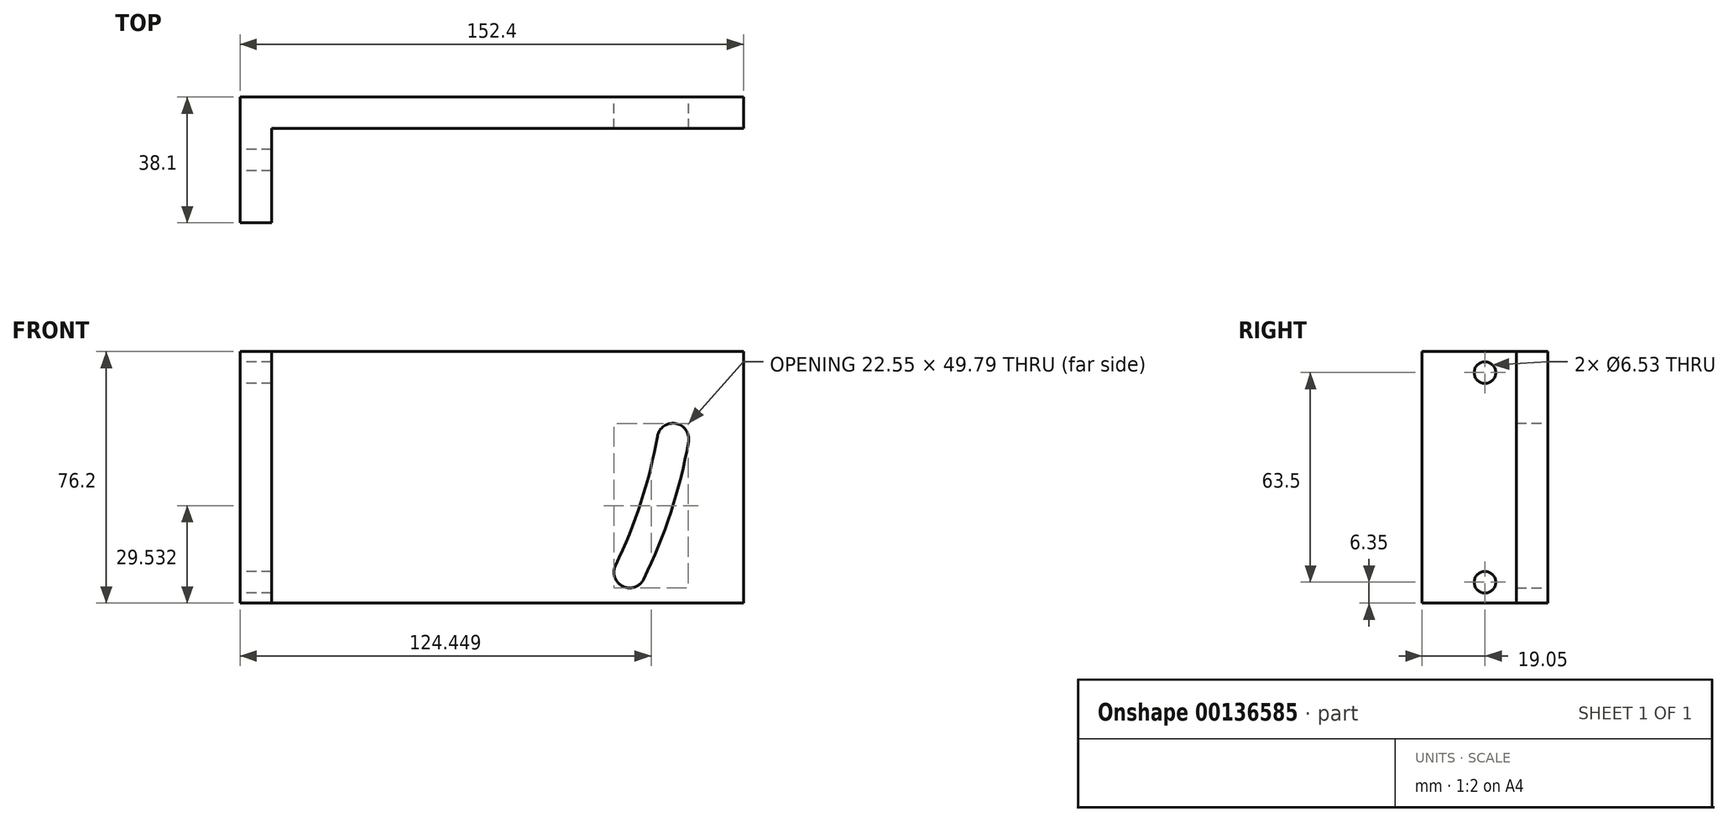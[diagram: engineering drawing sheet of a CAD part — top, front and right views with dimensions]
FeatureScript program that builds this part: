
annotation { "Feature Type Name" : "Feature", "Feature Type Description" : "" }
export const myFeature = defineFeature(function(context is Context, id is Id, definition is map)
    precondition{}
    {
        {
            var Q0;
            Q0=qCreatedBy(makeId("Front.planeOp"),FACE);
            var sketch = newSketch(context, id + "F0", { "sketchPlane" : qUnion([Q0])});
            skLineSegment(sketch, "E0.bottom", {"start": v(0, 0) * mm, "end": v(152.4, 0) * mm});
            skLineSegment(sketch, "E0.top", {"start": v(0, 76.2) * mm, "end": v(152.4, 76.2) * mm});
            skLineSegment(sketch, "E0.left", {"start": v(0, 0) * mm, "end": v(0, 76.2) * mm});
            skLineSegment(sketch, "E0.right", {"start": v(152.4, 0) * mm, "end": v(152.4, 76.2) * mm});
            skLineSegment(sketch, "E1", {"start": v(76.2, 76.2) * mm, "end": v(76.2, 0) * mm, "construction": true});
            skArc(sketch, "E2", {"start": v(117.93, 9.4) * mm, "mid": v(125.9, 29.1) * mm, "end": v(131.03, 49.74) * mm, "construction": true});
            skLineSegment(sketch, "E3", {"start": v(-19.05, 76.2) * mm, "end": v(-19.05, -76.2) * mm, "construction": true});
            skPoint(sketch, "E4.endSnap0", {"position": v(76.2, 38.1) * mm});
            skLineSegment(sketch, "E5", {"start": v(-19.05, 76.2) * mm, "end": v(125.9, 29.1) * mm, "construction": true});
            skLineSegment(sketch, "E6", {"start": v(-19.05, 76.2) * mm, "end": v(131.03, 49.74) * mm, "construction": true});
            skLineSegment(sketch, "E7", {"start": v(-19.05, 76.2) * mm, "end": v(117.93, 9.4) * mm, "construction": true});
            skArc(sketch, "E8.0.startCap", {"start": v(122.2, 7.3) * mm, "mid": v(115.84, 5.11) * mm, "end": v(113.65, 11.48) * mm});
            skArc(sketch, "E8.0.endCap", {"start": v(126.34, 50.56) * mm, "mid": v(131.86, 54.43) * mm, "end": v(135.72, 48.9) * mm});
            skArc(sketch, "E8.0.left", {"start": v(113.65, 11.48) * mm, "mid": v(121.36, 30.58) * mm, "end": v(126.34, 50.56) * mm});
            skArc(sketch, "E8.0.right", {"start": v(122.2, 7.3) * mm, "mid": v(130.42, 27.63) * mm, "end": v(135.72, 48.9) * mm});
            skSolve(sketch);
        }
        {
            var Q0;
            Q0=makeQuery(id+"F0.imprint","IMPRINT",FACE,{"disambiguationData":[TD([[makeQuery(id+"F0.imprint","IMPRINT",EDGE,{"derivedFrom":sQuery(id+"F0.wireOp",EDGE,"E0.bottom")}),1.0]])]});
            extrude(context, id + "F1", {"entities" : qUnion([Q0]), "depth" : 9.52 * mm});
        }
        {
            var Q0;
            Q0=makeQuery(id+"F1.opExtrude","CAP_FACE",FACE,{"disambiguationData":[OSD([sQuery(id+"F0.wireOp",EDGE,"E0.bottom"),sQuery(id+"F0.wireOp",EDGE,"E0.top"),sQuery(id+"F0.wireOp",EDGE,"E0.left"),sQuery(id+"F0.wireOp",EDGE,"E0.right"),sQuery(id+"F0.wireOp",EDGE,"E8.0.startCap"),sQuery(id+"F0.wireOp",EDGE,"E8.0.endCap"),sQuery(id+"F0.wireOp",EDGE,"E8.0.left"),sQuery(id+"F0.wireOp",EDGE,"E8.0.right")])],"isStart":false});
            var sketch = newSketch(context, id + "F2", { "sketchPlane" : qUnion([Q0])});
            skLineSegment(sketch, "E9.bottom", {"start": v(0, 0) * mm, "end": v(9.53, 0) * mm});
            skLineSegment(sketch, "E9.top", {"start": v(0, 76.2) * mm, "end": v(9.52, 76.2) * mm});
            skLineSegment(sketch, "E9.left", {"start": v(0, 0) * mm, "end": v(0, 76.2) * mm});
            skLineSegment(sketch, "E9.right", {"start": v(9.53, 0) * mm, "end": v(9.52, 76.2) * mm});
            skSolve(sketch);
        }
        {
            var Q0;
            Q0=makeQuery(id+"F2.imprint","IMPRINT",FACE,{"disambiguationData":[TD([[makeQuery(id+"F2.imprint","IMPRINT",EDGE,{"derivedFrom":sQuery(id+"F2.wireOp",EDGE,"E9.bottom")}),1.0]])]});
            extrude(context, id + "F3", {"entities" : qUnion([Q0]), "operationType" : NewBodyOperationType.ADD, "depth" : 28.57 * mm});
        }
        {
            var Q0;
            Q0=makeQuery(id+"F3.boolean.opBoolean","MERGE",FACE,{"derivedFrom":[makeQuery(id+"F1.opExtrude","SWEPT_FACE",FACE,{"disambiguationData":[OSD([sQuery(id+"F0.wireOp",EDGE,"E0.left")])]}),makeQuery(id+"F3.opExtrude","SWEPT_FACE",FACE,{"disambiguationData":[OSD([sQuery(id+"F2.wireOp",EDGE,"E9.left")])]})]});
            var sketch = newSketch(context, id + "F4", { "sketchPlane" : qUnion([Q0])});
            skLineSegment(sketch, "E10", {"start": v(19.05, 76.2) * mm, "end": v(19.05, 0) * mm, "construction": true});
            skPoint(sketch, "E11", {"position": v(19.05, 69.85) * mm});
            skPoint(sketch, "E12", {"position": v(19.05, 6.35) * mm});
            skSolve(sketch);
        }
        {
            var Q0;
            Q0=sQuery(id+"F4.wireOp",VERTEX,"E11");
            var Q1;
            Q1=sQuery(id+"F4.wireOp",VERTEX,"E12");
            var Q2;
            Q2=makeQuery(id+"F1.opExtrude","SWEPT_BODY",BODY,{"disambiguationData":[OSD([sQuery(id+"F0.wireOp",EDGE,"E0.bottom"),sQuery(id+"F0.wireOp",EDGE,"E0.top"),sQuery(id+"F0.wireOp",EDGE,"E0.left"),sQuery(id+"F0.wireOp",EDGE,"E0.right"),sQuery(id+"F0.wireOp",EDGE,"E8.0.startCap"),sQuery(id+"F0.wireOp",EDGE,"E8.0.endCap"),sQuery(id+"F0.wireOp",EDGE,"E8.0.left"),sQuery(id+"F0.wireOp",EDGE,"E8.0.right")])]});
            hole(context, id + "F5", {"style" : HoleStyle.SIMPLE, "endStyle" : HoleEndStyle.THROUGH, "holeDiameter" : 6.53 * mm, "locations" : qUnion([Q0, Q1]), "scope" : qUnion([Q2]), "isTappedThrough" : true});
        }
    });
